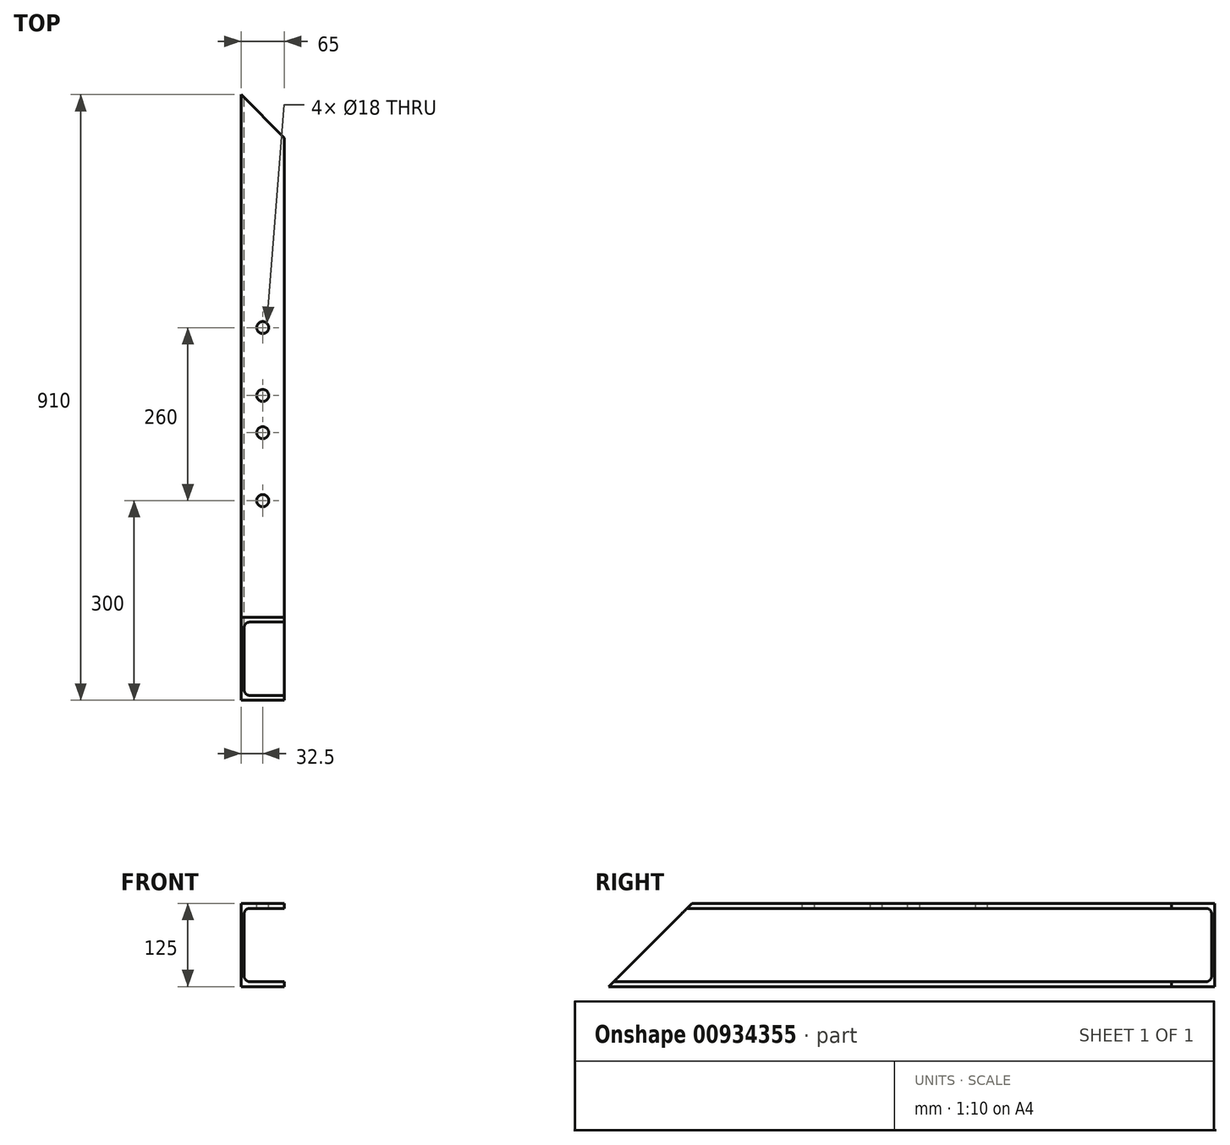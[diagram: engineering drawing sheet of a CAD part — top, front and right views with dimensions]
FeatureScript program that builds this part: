
annotation { "Feature Type Name" : "Feature", "Feature Type Description" : "" }
export const myFeature = defineFeature(function(context is Context, id is Id, definition is map)
    precondition{}
    {
        {
            var Q0;
            Q0=qCreatedBy(makeId("Front.planeOp"),FACE);
            var sketch = newSketch(context, id + "F0", { "sketchPlane" : qUnion([Q0])});
            skLineSegment(sketch, "E0", {"start": v(0, 0) * mm, "end": v(0, 125) * mm});
            skLineSegment(sketch, "E1", {"start": v(0, 125) * mm, "end": v(65, 125) * mm});
            skLineSegment(sketch, "E2", {"start": v(65, 125) * mm, "end": v(65, 117.5) * mm});
            skLineSegment(sketch, "E3", {"start": v(65, 117.5) * mm, "end": v(12.7, 117.5) * mm});
            skLineSegment(sketch, "E4", {"start": v(0, 0) * mm, "end": v(65, 0) * mm});
            skLineSegment(sketch, "E5", {"start": v(65, 0) * mm, "end": v(65, 7.5) * mm});
            skLineSegment(sketch, "E6", {"start": v(65, 7.5) * mm, "end": v(12.7, 7.5) * mm});
            skLineSegment(sketch, "E7", {"start": v(4.7, 15.5) * mm, "end": v(4.7, 109.5) * mm});
            skPoint(sketch, "E8.visualSharp", {"position": v(4.7, 117.5) * mm});
            skArc(sketch, "E8.filletArc", {"start": v(12.7, 117.5) * mm, "mid": v(7.04, 115.16) * mm, "end": v(4.7, 109.5) * mm});
            skPoint(sketch, "E9.visualSharp", {"position": v(4.7, 7.5) * mm});
            skArc(sketch, "E9.filletArc", {"start": v(4.7, 15.5) * mm, "mid": v(7.04, 9.84) * mm, "end": v(12.7, 7.5) * mm});
            skSolve(sketch);
        }
        {
            var Q0;
            Q0=makeQuery(id+"F0.imprint","IMPRINT",FACE,{"disambiguationData":[TD([[makeQuery(id+"F0.imprint","IMPRINT",EDGE,{"derivedFrom":sQuery(id+"F0.wireOp",EDGE,"E0")}),-1.0]])]});
            extrude(context, id + "F1", {"entities" : qUnion([Q0]), "depth" : 910 * mm, "offsetDistance" : 25 * mm});
        }
        {
            var Q0;
            Q0=makeQuery(id+"F1.opExtrude","SWEPT_FACE",FACE,{"disambiguationData":[OSD([sQuery(id+"F0.wireOp",EDGE,"E1")])]});
            var sketch = newSketch(context, id + "F2", { "sketchPlane" : qUnion([Q0])});
            skLineSegment(sketch, "E10", {"start": v(65, 0) * mm, "end": v(65, -65) * mm});
            skLineSegment(sketch, "E11", {"start": v(65, -65) * mm, "end": v(0, 0) * mm});
            skSolve(sketch);
        }
        {
            var Q0;
            Q0=makeQuery(id+"F2.imprint","IMPRINT",FACE,{"disambiguationData":[TD([[makeQuery(id+"F2.imprint","IMPRINT",EDGE,{"derivedFrom":sQuery(id+"F2.wireOp",EDGE,"E10")}),1.0]])]});
            extrude(context, id + "F3", {"entities" : qUnion([Q0]), "operationType" : NewBodyOperationType.REMOVE, "endBound" : BoundingType.THROUGH_ALL, "oppositeDirection" : true, "depth" : 25 * mm, "offsetDistance" : 25 * mm});
        }
        {
            var Q0;
            Q0=makeQuery(id+"F1.opExtrude","SWEPT_FACE",FACE,{"disambiguationData":[OSD([sQuery(id+"F0.wireOp",EDGE,"E0")])]});
            var sketch = newSketch(context, id + "F4", { "sketchPlane" : qUnion([Q0])});
            skLineSegment(sketch, "E12", {"start": v(910, 125) * mm, "end": v(785, 125) * mm});
            skLineSegment(sketch, "E13", {"start": v(785, 125) * mm, "end": v(910, 0) * mm});
            skSolve(sketch);
        }
        {
            var Q0;
            Q0=makeQuery(id+"F4.imprint","IMPRINT",FACE,{"disambiguationData":[TD([[makeQuery(id+"F4.imprint","IMPRINT",EDGE,{"derivedFrom":sQuery(id+"F4.wireOp",EDGE,"E12")}),1.0]])]});
            extrude(context, id + "F5", {"entities" : qUnion([Q0]), "operationType" : NewBodyOperationType.REMOVE, "endBound" : BoundingType.THROUGH_ALL, "oppositeDirection" : true, "depth" : 25 * mm, "offsetDistance" : 25 * mm});
        }
        {
            var Q0;
            Q0=makeQuery(id+"F1.opExtrude","SWEPT_FACE",FACE,{"disambiguationData":[OSD([sQuery(id+"F0.wireOp",EDGE,"E1")])]});
            var sketch = newSketch(context, id + "F6", { "sketchPlane" : qUnion([Q0])});
            skCircle(sketch, "E14", {"center": v(32.5, -350) * mm, "radius": 9 * mm});
            skCircle(sketch, "E15", {"center": v(32.5, -452) * mm, "radius": 9 * mm});
            skSolve(sketch);
        }
        {
            var Q0;
            Q0 = qSketchRegion(id + "F6", true);
            extrude(context, id + "F7", {"entities" : qUnion([Q0]), "operationType" : NewBodyOperationType.REMOVE, "endBound" : BoundingType.UP_TO_NEXT, "oppositeDirection" : true, "depth" : 25 * mm, "offsetDistance" : 25 * mm});
        }
        {
            var Q0;
            Q0=makeQuery(id+"F1.opExtrude","SWEPT_FACE",FACE,{"disambiguationData":[OSD([sQuery(id+"F0.wireOp",EDGE,"E1")])]});
            var sketch = newSketch(context, id + "F8", { "sketchPlane" : qUnion([Q0])});
            skCircle(sketch, "E16", {"center": v(32.5, -508) * mm, "radius": 9 * mm});
            skCircle(sketch, "E17", {"center": v(32.5, -610) * mm, "radius": 9 * mm});
            skLineSegment(sketch, "E18", {"start": v(32.5, -508) * mm, "end": v(32.5, -610) * mm, "construction": true});
            skLineSegment(sketch, "E19", {"start": v(32.5, -610) * mm, "end": v(32.5, -785) * mm, "construction": true});
            skSolve(sketch);
        }
        {
            var Q0;
            Q0 = qSketchRegion(id + "F8", true);
            extrude(context, id + "F9", {"entities" : qUnion([Q0]), "operationType" : NewBodyOperationType.REMOVE, "endBound" : BoundingType.UP_TO_NEXT, "oppositeDirection" : true, "depth" : 25 * mm, "offsetDistance" : 25 * mm});
        }
    });
